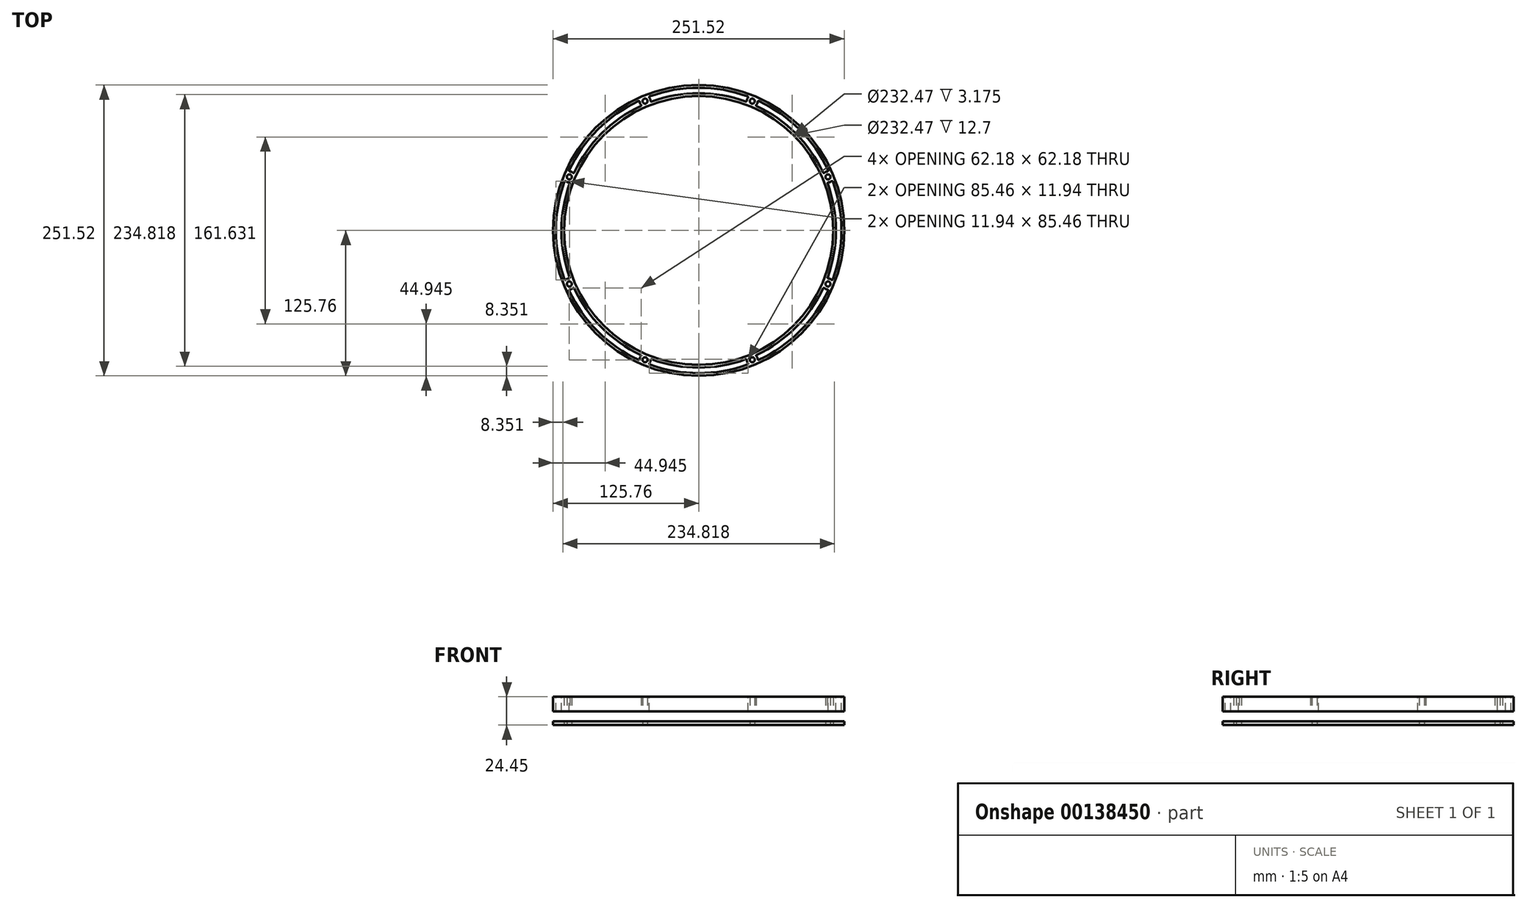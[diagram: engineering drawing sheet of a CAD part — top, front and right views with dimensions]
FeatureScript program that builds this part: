
annotation { "Feature Type Name" : "Feature", "Feature Type Description" : "" }
export const myFeature = defineFeature(function(context is Context, id is Id, definition is map)
    precondition{}
    {
        {
            var Q0;
            Q0=qCreatedBy(makeId("Top.planeOp"),FACE);
            var sketch = newSketch(context, id + "F0", { "sketchPlane" : qUnion([Q0])});
            skCircle(sketch, "E0", {"center": v(0, 0) * mm, "radius": 125.76 * mm});
            skCircle(sketch, "E1.cCircle", {"center": v(0, 0) * mm, "radius": 111.79 * mm, "construction": true});
            skLineSegment(sketch, "E1.0", {"start": v(46.3, -111.79) * mm, "end": v(-46.3, -111.79) * mm, "construction": true});
            skLineSegment(sketch, "E1.1", {"start": v(-46.3, -111.79) * mm, "end": v(-111.79, -46.3) * mm, "construction": true});
            skLineSegment(sketch, "E1.2", {"start": v(-111.79, -46.3) * mm, "end": v(-111.79, 46.3) * mm, "construction": true});
            skLineSegment(sketch, "E1.3", {"start": v(-111.79, 46.3) * mm, "end": v(-46.3, 111.79) * mm, "construction": true});
            skLineSegment(sketch, "E1.4", {"start": v(-46.3, 111.79) * mm, "end": v(46.3, 111.79) * mm, "construction": true});
            skLineSegment(sketch, "E1.5", {"start": v(46.3, 111.79) * mm, "end": v(111.79, 46.3) * mm, "construction": true});
            skLineSegment(sketch, "E1.6", {"start": v(111.79, 46.3) * mm, "end": v(111.79, -46.3) * mm, "construction": true});
            skLineSegment(sketch, "E1.7", {"start": v(111.79, -46.3) * mm, "end": v(46.3, -111.79) * mm, "construction": true});
            skCircle(sketch, "E2", {"center": v(-46.3, 111.79) * mm, "radius": 4.76 * mm, "construction": true});
            skCircle(sketch, "E3", {"center": v(0, 0) * mm, "radius": 116.24 * mm});
            skCircle(sketch, "E4", {"center": v(-46.3, 111.79) * mm, "radius": 2.15 * mm});
            skCircle(sketch, "E5", {"center": v(46.3, 111.79) * mm, "radius": 2.15 * mm});
            skCircle(sketch, "E6", {"center": v(111.79, 46.3) * mm, "radius": 2.15 * mm});
            skCircle(sketch, "E7", {"center": v(111.79, -46.3) * mm, "radius": 2.15 * mm});
            skCircle(sketch, "E8", {"center": v(46.3, -111.79) * mm, "radius": 2.15 * mm});
            skCircle(sketch, "E9", {"center": v(-46.3, -111.79) * mm, "radius": 2.15 * mm});
            skCircle(sketch, "E10", {"center": v(-111.79, -46.3) * mm, "radius": 2.15 * mm});
            skCircle(sketch, "E11", {"center": v(-111.79, 46.3) * mm, "radius": 2.15 * mm});
            skSolve(sketch);
        }
        {
            var Q0;
            Q0=qSketchRegion(id+"F0",true);
            extrude(context, id + "F1", {"entities" : qUnion([Q0]), "depth" : 12.7 * mm});
        }
        {
            var Q0;
            Q0=makeQuery(id+"F1.opExtrude","CAP_FACE",FACE,{"disambiguationData":[OSD([sQuery(id+"F0.wireOp",EDGE,"E0"),sQuery(id+"F0.wireOp",EDGE,"E3"),sQuery(id+"F0.wireOp",EDGE,"E4"),sQuery(id+"F0.wireOp",EDGE,"E5"),sQuery(id+"F0.wireOp",EDGE,"E6"),sQuery(id+"F0.wireOp",EDGE,"E7"),sQuery(id+"F0.wireOp",EDGE,"E8"),sQuery(id+"F0.wireOp",EDGE,"E9"),sQuery(id+"F0.wireOp",EDGE,"E10"),sQuery(id+"F0.wireOp",EDGE,"E11")])],"isStart":false});
            var sketch = newSketch(context, id + "F2", { "sketchPlane" : qUnion([Q0])});
            skArc(sketch, "E12", {"start": v(-107.96, 49.14) * mm, "mid": v(-109.9, 50.67) * mm, "end": v(-112.33, 51.04) * mm});
            skArc(sketch, "E13", {"start": v(-49.14, 107.96) * mm, "mid": v(-83.88, 83.88) * mm, "end": v(-107.96, 49.14) * mm});
            skArc(sketch, "E14", {"start": v(-51.04, 112.33) * mm, "mid": v(-50.67, 109.9) * mm, "end": v(-49.14, 107.96) * mm});
            skArc(sketch, "E15", {"start": v(-51.04, 112.33) * mm, "mid": v(-87.24, 87.24) * mm, "end": v(-112.33, 51.04) * mm});
            skSolve(sketch);
        }
        {
            var Q0;
            Q0=qSketchRegion(id+"F2",true);
            var Q1;
            Q1=makeQuery(id+"F1.opExtrude","CAP_FACE",FACE,{"disambiguationData":[OSD([sQuery(id+"F0.wireOp",EDGE,"E0"),sQuery(id+"F0.wireOp",EDGE,"E3"),sQuery(id+"F0.wireOp",EDGE,"E4"),sQuery(id+"F0.wireOp",EDGE,"E5"),sQuery(id+"F0.wireOp",EDGE,"E6"),sQuery(id+"F0.wireOp",EDGE,"E7"),sQuery(id+"F0.wireOp",EDGE,"E8"),sQuery(id+"F0.wireOp",EDGE,"E9"),sQuery(id+"F0.wireOp",EDGE,"E10"),sQuery(id+"F0.wireOp",EDGE,"E11")])],"isStart":true});
            extrude(context, id + "F3", {"entities" : qUnion([Q0]), "operationType" : NewBodyOperationType.REMOVE, "endBound" : BoundingType.UP_TO_SURFACE, "oppositeDirection" : true, "endBoundEntityFace" : qUnion([Q1]), "depth" : 25.4 * mm});
        }
        {
            var Q0;
            {var subQ0=sQuery(id+"F2.wireOp",EDGE,"E13");var subQ1=sQuery(id+"F2.wireOp",EDGE,"E14");Q0=makeQuery(id+"F8.boolean.opBoolean","SPLIT",EDGE,{"disambiguationData":[TD([makeQuery(id+"F1.opExtrude","CAP_FACE",FACE,{"disambiguationData":[OSD([sQuery(id+"F0.wireOp",EDGE,"E0"),sQuery(id+"F0.wireOp",EDGE,"E3"),sQuery(id+"F0.wireOp",EDGE,"E4"),sQuery(id+"F0.wireOp",EDGE,"E5"),sQuery(id+"F0.wireOp",EDGE,"E6"),sQuery(id+"F0.wireOp",EDGE,"E7"),sQuery(id+"F0.wireOp",EDGE,"E8"),sQuery(id+"F0.wireOp",EDGE,"E9"),sQuery(id+"F0.wireOp",EDGE,"E10"),sQuery(id+"F0.wireOp",EDGE,"E11")])],"isStart":false})])],"derivedFrom":makeQuery(id+"F3.boolean.opBoolean","COPY",EDGE,{"derivedFrom":makeQuery(id+"F3.opExtrude","SWEPT_EDGE",EDGE,{"disambiguationData":[OSD([subQ0,subQ1])]})})});}
            var Q1;
            {var subQ0=sQuery(id+"F2.wireOp",EDGE,"E14");var subQ1=sQuery(id+"F2.wireOp",EDGE,"E15");Q1=makeQuery(id+"F8.boolean.opBoolean","SPLIT",EDGE,{"disambiguationData":[TD([makeQuery(id+"F1.opExtrude","CAP_FACE",FACE,{"disambiguationData":[OSD([sQuery(id+"F0.wireOp",EDGE,"E0"),sQuery(id+"F0.wireOp",EDGE,"E3"),sQuery(id+"F0.wireOp",EDGE,"E4"),sQuery(id+"F0.wireOp",EDGE,"E5"),sQuery(id+"F0.wireOp",EDGE,"E6"),sQuery(id+"F0.wireOp",EDGE,"E7"),sQuery(id+"F0.wireOp",EDGE,"E8"),sQuery(id+"F0.wireOp",EDGE,"E9"),sQuery(id+"F0.wireOp",EDGE,"E10"),sQuery(id+"F0.wireOp",EDGE,"E11")])],"isStart":false})])],"derivedFrom":makeQuery(id+"F3.boolean.opBoolean","COPY",EDGE,{"derivedFrom":makeQuery(id+"F3.opExtrude","SWEPT_EDGE",EDGE,{"disambiguationData":[OSD([subQ0,subQ1])]})})});}
            var Q2;
            {var subQ0=sQuery(id+"F2.wireOp",EDGE,"E12");var subQ1=sQuery(id+"F2.wireOp",EDGE,"E13");Q2=makeQuery(id+"F8.boolean.opBoolean","SPLIT",EDGE,{"disambiguationData":[TD([makeQuery(id+"F1.opExtrude","CAP_FACE",FACE,{"disambiguationData":[OSD([sQuery(id+"F0.wireOp",EDGE,"E0"),sQuery(id+"F0.wireOp",EDGE,"E3"),sQuery(id+"F0.wireOp",EDGE,"E4"),sQuery(id+"F0.wireOp",EDGE,"E5"),sQuery(id+"F0.wireOp",EDGE,"E6"),sQuery(id+"F0.wireOp",EDGE,"E7"),sQuery(id+"F0.wireOp",EDGE,"E8"),sQuery(id+"F0.wireOp",EDGE,"E9"),sQuery(id+"F0.wireOp",EDGE,"E10"),sQuery(id+"F0.wireOp",EDGE,"E11")])],"isStart":false})])],"derivedFrom":makeQuery(id+"F3.boolean.opBoolean","COPY",EDGE,{"derivedFrom":makeQuery(id+"F3.opExtrude","SWEPT_EDGE",EDGE,{"disambiguationData":[OSD([subQ0,subQ1])]})})});}
            var Q3;
            {var subQ0=sQuery(id+"F2.wireOp",EDGE,"E12");var subQ1=sQuery(id+"F2.wireOp",EDGE,"E15");Q3=makeQuery(id+"F8.boolean.opBoolean","SPLIT",EDGE,{"disambiguationData":[TD([makeQuery(id+"F1.opExtrude","CAP_FACE",FACE,{"disambiguationData":[OSD([sQuery(id+"F0.wireOp",EDGE,"E0"),sQuery(id+"F0.wireOp",EDGE,"E3"),sQuery(id+"F0.wireOp",EDGE,"E4"),sQuery(id+"F0.wireOp",EDGE,"E5"),sQuery(id+"F0.wireOp",EDGE,"E6"),sQuery(id+"F0.wireOp",EDGE,"E7"),sQuery(id+"F0.wireOp",EDGE,"E8"),sQuery(id+"F0.wireOp",EDGE,"E9"),sQuery(id+"F0.wireOp",EDGE,"E10"),sQuery(id+"F0.wireOp",EDGE,"E11")])],"isStart":false})])],"derivedFrom":makeQuery(id+"F3.boolean.opBoolean","COPY",EDGE,{"derivedFrom":makeQuery(id+"F3.opExtrude","SWEPT_EDGE",EDGE,{"disambiguationData":[OSD([subQ0,subQ1])]})})});}
            fillet(context, id + "F4", {"entities" : qUnion([Q0, Q1, Q2, Q3]), "radius" : 0.76 * mm, "tangentPropagation" : true, "allowEdgeOverflow" : false});
        }
        {
            var Q0;
            Q0=makeQuery(id+"F4.opFillet","BLEND_FACE",FACE,{"disambiguationData":[OSD([sQuery(id+"F2.wireOp",EDGE,"E13"),sQuery(id+"F2.wireOp",EDGE,"E14")])]});
            var Q1;
            Q1=makeQuery(id+"F3.boolean.opBoolean","COPY",FACE,{"derivedFrom":makeQuery(id+"F3.opExtrude","SWEPT_FACE",FACE,{"disambiguationData":[OSD([sQuery(id+"F2.wireOp",EDGE,"E14")])]})});
            var Q2;
            Q2=makeQuery(id+"F4.opFillet","BLEND_FACE",FACE,{"disambiguationData":[OSD([sQuery(id+"F2.wireOp",EDGE,"E14"),sQuery(id+"F2.wireOp",EDGE,"E15")])]});
            var Q3;
            Q3=makeQuery(id+"F3.boolean.opBoolean","COPY",FACE,{"derivedFrom":makeQuery(id+"F3.opExtrude","SWEPT_FACE",FACE,{"disambiguationData":[OSD([sQuery(id+"F2.wireOp",EDGE,"E15")])]})});
            var Q4;
            Q4=makeQuery(id+"F3.boolean.opBoolean","COPY",FACE,{"derivedFrom":makeQuery(id+"F3.opExtrude","SWEPT_FACE",FACE,{"disambiguationData":[OSD([sQuery(id+"F2.wireOp",EDGE,"E13")])]})});
            var Q5;
            Q5=makeQuery(id+"F4.opFillet","BLEND_FACE",FACE,{"disambiguationData":[OSD([sQuery(id+"F2.wireOp",EDGE,"E12"),sQuery(id+"F2.wireOp",EDGE,"E13")])]});
            var Q6;
            Q6=makeQuery(id+"F3.boolean.opBoolean","COPY",FACE,{"derivedFrom":makeQuery(id+"F3.opExtrude","SWEPT_FACE",FACE,{"disambiguationData":[OSD([sQuery(id+"F2.wireOp",EDGE,"E12")])]})});
            var Q7;
            Q7=makeQuery(id+"F4.opFillet","BLEND_FACE",FACE,{"disambiguationData":[OSD([sQuery(id+"F2.wireOp",EDGE,"E12"),sQuery(id+"F2.wireOp",EDGE,"E15")])]});
            var Q8;
            Q8=makeQuery(id+"F1.opExtrude","SWEPT_FACE",FACE,{"disambiguationData":[OSD([sQuery(id+"F0.wireOp",EDGE,"E3")])]});
            circularPattern(context, id + "F5", {"patternType" : PatternType.FACE, "faces" : qUnion([Q0, Q1, Q2, Q3, Q4, Q5, Q6, Q7]), "axis" : qUnion([Q8]), "angle" : 45 * degree, "instanceCount" : 8});
        }
        {
            var Q0;
            Q0=makeQuery(id+"F1.opExtrude","CAP_FACE",FACE,{"disambiguationData":[OSD([sQuery(id+"F0.wireOp",EDGE,"E0"),sQuery(id+"F0.wireOp",EDGE,"E3"),sQuery(id+"F0.wireOp",EDGE,"E4"),sQuery(id+"F0.wireOp",EDGE,"E5"),sQuery(id+"F0.wireOp",EDGE,"E6"),sQuery(id+"F0.wireOp",EDGE,"E7"),sQuery(id+"F0.wireOp",EDGE,"E8"),sQuery(id+"F0.wireOp",EDGE,"E9"),sQuery(id+"F0.wireOp",EDGE,"E10"),sQuery(id+"F0.wireOp",EDGE,"E11")])],"isStart":false});
            cPlane(context, id + "F6", {"entities" : qUnion([Q0]), "cplaneType" : CPlaneType.OFFSET, "offset" : 22.86 * mm, "oppositeDirection" : true, "width" : 152.4 * mm, "height" : 152.4 * mm});
        }
        {
            var Q0;
            Q0=qCreatedBy(id+"F6.planeOp",FACE);
            var sketch = newSketch(context, id + "F7", { "sketchPlane" : qUnion([Q0])});
            skCircle(sketch, "E16", {"center": v(0, 0) * mm, "radius": 125.76 * mm});
            skCircle(sketch, "E17", {"center": v(0, 0) * mm, "radius": 116.24 * mm});
            skCircle(sketch, "E18", {"center": v(-46.3, 111.79) * mm, "radius": 2.15 * mm});
            skCircle(sketch, "E19", {"center": v(46.3, 111.79) * mm, "radius": 2.15 * mm});
            skCircle(sketch, "E20", {"center": v(111.79, 46.3) * mm, "radius": 2.15 * mm});
            skCircle(sketch, "E21", {"center": v(-46.3, -111.79) * mm, "radius": 2.15 * mm});
            skCircle(sketch, "E22", {"center": v(111.79, -46.3) * mm, "radius": 2.15 * mm});
            skCircle(sketch, "E23", {"center": v(46.3, -111.79) * mm, "radius": 2.15 * mm});
            skCircle(sketch, "E24", {"center": v(-111.79, -46.3) * mm, "radius": 2.15 * mm});
            skCircle(sketch, "E25", {"center": v(-111.79, 46.3) * mm, "radius": 2.15 * mm});
            skSolve(sketch);
        }
        {
            var Q0;
            Q0=qSketchRegion(id+"F7",true);
            extrude(context, id + "F8", {"entities" : qUnion([Q0]), "operationType" : NewBodyOperationType.ADD, "endBound" : BoundingType.SYMMETRIC, "depth" : 3.17 * mm});
        }
    });
